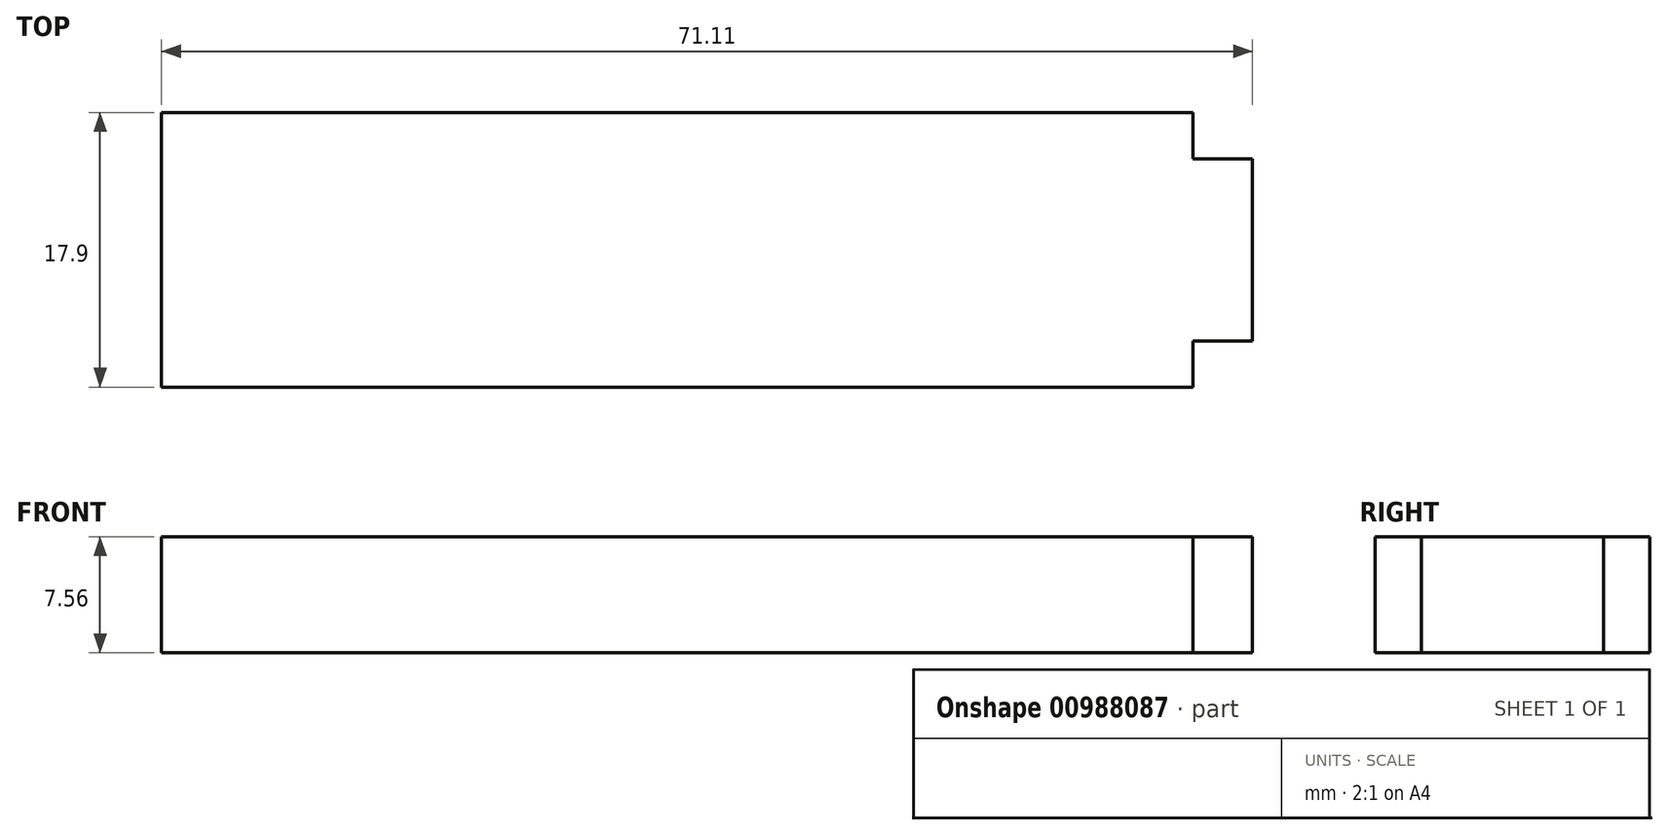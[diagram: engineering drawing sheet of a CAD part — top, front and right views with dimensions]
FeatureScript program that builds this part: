
annotation { "Feature Type Name" : "Feature", "Feature Type Description" : "" }
export const myFeature = defineFeature(function(context is Context, id is Id, definition is map)
    precondition{}
    {
        {
            var Q0;
            Q0=qCreatedBy(makeId("Top.planeOp"),FACE);
            var sketch = newSketch(context, id + "F0", { "sketchPlane" : qUnion([Q0])});
            skLineSegment(sketch, "E0.bottom", {"start": v(33.62, -8.95) * mm, "end": v(-33.62, -8.95) * mm});
            skLineSegment(sketch, "E0.top", {"start": v(33.62, 8.95) * mm, "end": v(-33.62, 8.95) * mm});
            skLineSegment(sketch, "E0.left", {"start": v(33.62, -8.95) * mm, "end": v(33.62, 8.95) * mm});
            skLineSegment(sketch, "E0.right", {"start": v(-33.62, -8.95) * mm, "end": v(-33.62, 8.95) * mm});
            skPoint(sketch, "E0.middle", {"position": v(0, 0) * mm});
            skSolve(sketch);
        }
        {
            var Q0;
            Q0 = qSketchRegion(id + "F0", true);
            extrude(context, id + "F1", {"entities" : qUnion([Q0]), "endBound" : BoundingType.SYMMETRIC, "depth" : 7.56 * mm, "offsetDistance" : 25 * mm});
        }
        {
            var Q0;
            Q0=makeQuery(id+"F1.opExtrude","CAP_FACE",FACE,{"disambiguationData":[OSD([sQuery(id+"F0.wireOp",EDGE,"E0.bottom"),sQuery(id+"F0.wireOp",EDGE,"E0.top"),sQuery(id+"F0.wireOp",EDGE,"E0.left"),sQuery(id+"F0.wireOp",EDGE,"E0.right")])],"isStart":false});
            var sketch = newSketch(context, id + "F2", { "sketchPlane" : qUnion([Q0])});
            skLineSegment(sketch, "E1.bottom", {"start": v(33.62, 5.94) * mm, "end": v(37.49, 5.94) * mm});
            skLineSegment(sketch, "E1.top", {"start": v(33.62, -5.94) * mm, "end": v(37.49, -5.94) * mm});
            skLineSegment(sketch, "E1.left", {"start": v(33.62, 5.94) * mm, "end": v(33.62, -5.94) * mm});
            skLineSegment(sketch, "E1.right", {"start": v(37.49, 5.94) * mm, "end": v(37.49, -5.94) * mm});
            skPoint(sketch, "E2", {"position": v(33.62, 0) * mm});
            skSolve(sketch);
        }
        {
            var Q0;
            Q0 = qSketchRegion(id + "F2", true);
            var Q1;
            Q1=makeQuery(id+"F1.opExtrude","CAP_FACE",FACE,{"disambiguationData":[OSD([sQuery(id+"F0.wireOp",EDGE,"E0.bottom"),sQuery(id+"F0.wireOp",EDGE,"E0.top"),sQuery(id+"F0.wireOp",EDGE,"E0.left"),sQuery(id+"F0.wireOp",EDGE,"E0.right")])],"isStart":true});
            extrude(context, id + "F3", {"entities" : qUnion([Q0]), "operationType" : NewBodyOperationType.ADD, "endBound" : BoundingType.UP_TO_SURFACE, "oppositeDirection" : true, "depth" : 25 * mm, "endBoundEntityFace" : qUnion([Q1]), "offsetDistance" : 25 * mm});
        }
    });
